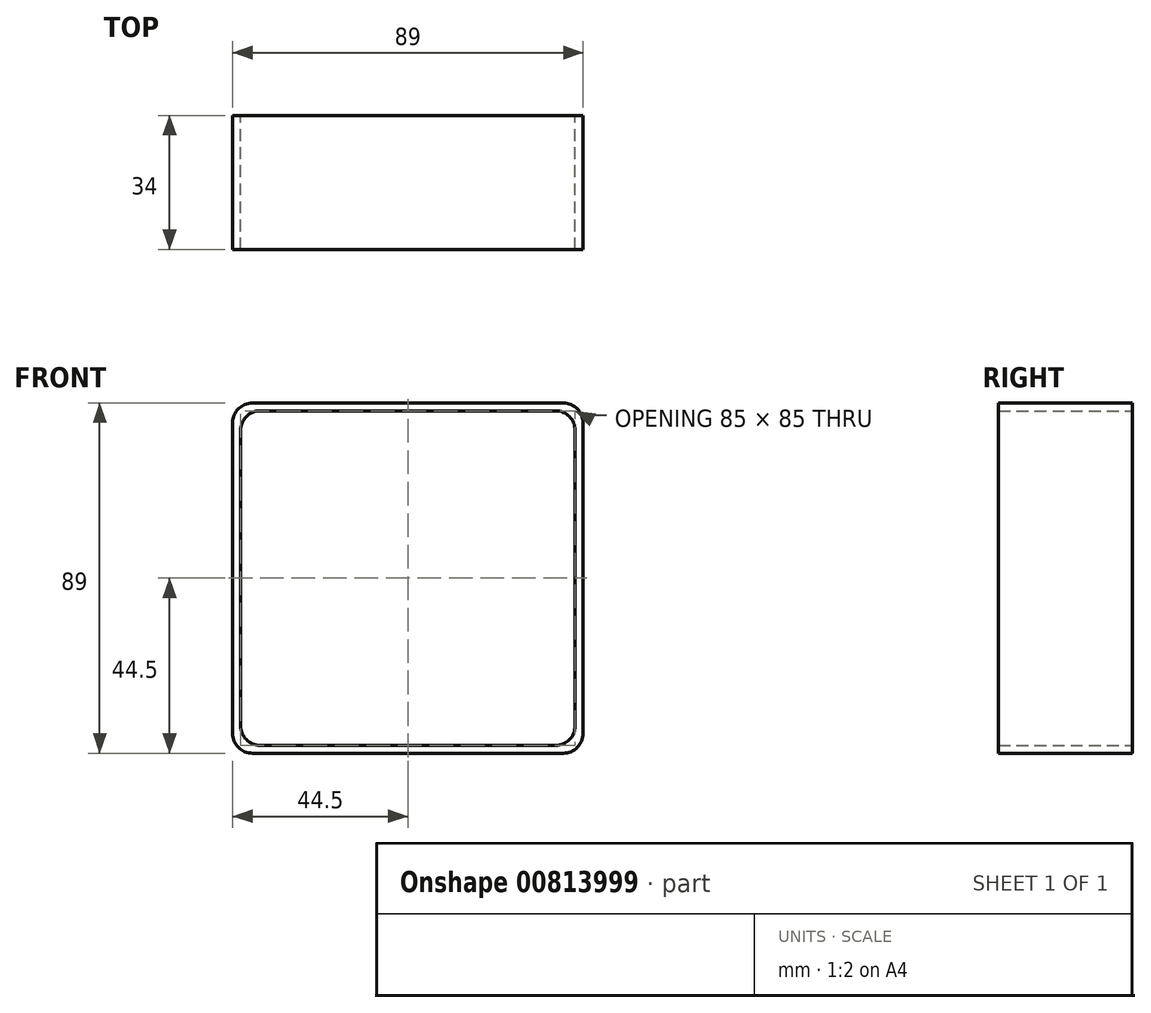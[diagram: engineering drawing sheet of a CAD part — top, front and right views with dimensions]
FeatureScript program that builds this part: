
annotation { "Feature Type Name" : "Feature", "Feature Type Description" : "" }
export const myFeature = defineFeature(function(context is Context, id is Id, definition is map)
    precondition{}
    {
        {
            var Q0;
            Q0=qCreatedBy(makeId("Front.planeOp"),FACE);
            var sketch = newSketch(context, id + "F0", { "sketchPlane" : qUnion([Q0])});
            skLineSegment(sketch, "E0.bottom", {"start": v(39.5, 44.5) * mm, "end": v(-39.5, 44.5) * mm});
            skLineSegment(sketch, "E0.top", {"start": v(39.5, -44.5) * mm, "end": v(-39.5, -44.5) * mm});
            skLineSegment(sketch, "E0.left", {"start": v(44.5, 39.5) * mm, "end": v(44.5, -39.5) * mm});
            skLineSegment(sketch, "E0.right", {"start": v(-44.5, 39.5) * mm, "end": v(-44.5, -39.5) * mm});
            skPoint(sketch, "E0.middle", {"position": v(0, 0) * mm});
            skPoint(sketch, "E1.visualSharp", {"position": v(-44.5, -44.5) * mm});
            skArc(sketch, "E1.filletArc", {"start": v(-44.5, -39.5) * mm, "mid": v(-43.04, -43.04) * mm, "end": v(-39.5, -44.5) * mm});
            skPoint(sketch, "E2.visualSharp", {"position": v(-44.5, 44.5) * mm});
            skArc(sketch, "E2.filletArc", {"start": v(-39.5, 44.5) * mm, "mid": v(-43.04, 43.04) * mm, "end": v(-44.5, 39.5) * mm});
            skPoint(sketch, "E3.visualSharp", {"position": v(44.5, 44.5) * mm});
            skArc(sketch, "E3.filletArc", {"start": v(44.5, 39.5) * mm, "mid": v(43.04, 43.04) * mm, "end": v(39.5, 44.5) * mm});
            skPoint(sketch, "E4.visualSharp", {"position": v(44.5, -44.5) * mm});
            skArc(sketch, "E4.filletArc", {"start": v(39.5, -44.5) * mm, "mid": v(43.04, -43.04) * mm, "end": v(44.5, -39.5) * mm});
            skLineSegment(sketch, "E5.bottom", {"start": v(37.5, 42.5) * mm, "end": v(-37.5, 42.5) * mm});
            skLineSegment(sketch, "E5.top", {"start": v(37.5, -42.5) * mm, "end": v(-37.5, -42.5) * mm});
            skLineSegment(sketch, "E5.left", {"start": v(42.5, 37.5) * mm, "end": v(42.5, -37.5) * mm});
            skLineSegment(sketch, "E5.right", {"start": v(-42.5, 37.5) * mm, "end": v(-42.5, -37.5) * mm});
            skPoint(sketch, "E6.visualSharp", {"position": v(-42.5, 42.5) * mm});
            skArc(sketch, "E6.filletArc", {"start": v(-37.5, 42.5) * mm, "mid": v(-41.04, 41.04) * mm, "end": v(-42.5, 37.5) * mm});
            skPoint(sketch, "E7.visualSharp", {"position": v(-42.5, -42.5) * mm});
            skArc(sketch, "E7.filletArc", {"start": v(-42.5, -37.5) * mm, "mid": v(-41.04, -41.04) * mm, "end": v(-37.5, -42.5) * mm});
            skPoint(sketch, "E8.visualSharp", {"position": v(42.5, -42.5) * mm});
            skArc(sketch, "E8.filletArc", {"start": v(37.5, -42.5) * mm, "mid": v(41.04, -41.04) * mm, "end": v(42.5, -37.5) * mm});
            skPoint(sketch, "E9.visualSharp", {"position": v(42.5, 42.5) * mm});
            skArc(sketch, "E9.filletArc", {"start": v(42.5, 37.5) * mm, "mid": v(41.04, 41.04) * mm, "end": v(37.5, 42.5) * mm});
            skSolve(sketch);
        }
        {
            var Q0;
            Q0=makeQuery(id+"F0.imprint","IMPRINT",FACE,{"disambiguationData":[TD([[makeQuery(id+"F0.imprint","IMPRINT",EDGE,{"derivedFrom":sQuery(id+"F0.wireOp",EDGE,"E0.bottom")}),1.0]])]});
            extrude(context, id + "F1", {"entities" : qUnion([Q0]), "depth" : 34 * mm, "offsetDistance" : 25 * mm});
        }
    });
